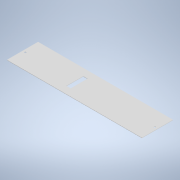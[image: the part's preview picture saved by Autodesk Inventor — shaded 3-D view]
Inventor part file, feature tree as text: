
AUTODESK INVENTOR PART (.ipt)
format: ipt  version: 2022 (Build 260153000, 153)  size: 106,496 bytes
history: native  units: mm
features: other x1, extrude x1, sketch x1
ambient origin geometry x8: Origin, YZ Plane, XZ Plane, XY Plane, X Axis, Y Axis, Z Axis, Center Point
bodies: Body1 (feature_tree)
feature tree (3):
  other  "Твердое тело1"
  extrude  "Выдавливание1"  Depth=0.5mm TaperAngle=0.0deg
  sketch  "Эскиз1"
